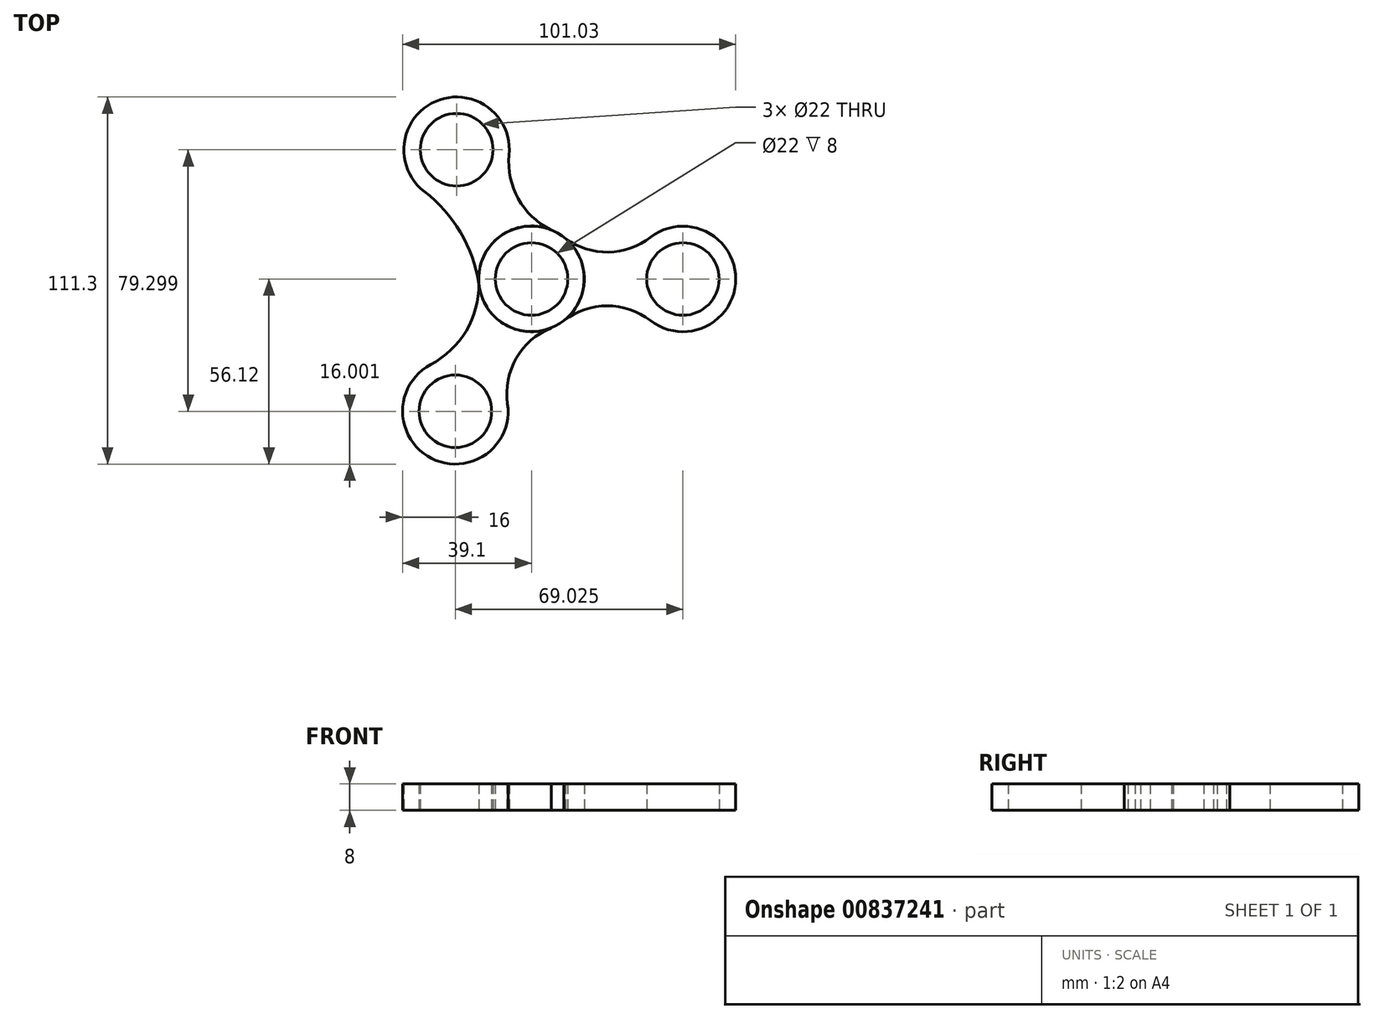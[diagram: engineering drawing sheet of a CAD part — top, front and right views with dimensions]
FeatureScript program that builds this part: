
annotation { "Feature Type Name" : "Feature", "Feature Type Description" : "" }
export const myFeature = defineFeature(function(context is Context, id is Id, definition is map)
    precondition{}
    {
        {
            var Q0;
            Q0=qCreatedBy(makeId("Top.planeOp"),FACE);
            var sketch = newSketch(context, id + "F0", { "sketchPlane" : qUnion([Q0])});
            skCircle(sketch, "E0", {"center": v(0, 0) * mm, "radius": 11 * mm});
            skCircle(sketch, "E1", {"center": v(45.93, 0) * mm, "radius": 11 * mm});
            skArc(sketch, "E2.0", {"start": v(36.13, -12.65) * mm, "mid": v(61.93, 0) * mm, "end": v(36.13, 12.65) * mm});
            skCircle(sketch, "E3.0", {"center": v(0, 0) * mm, "radius": 16 * mm});
            skArc(sketch, "E4", {"start": v(9.8, 12.65) * mm, "mid": v(22.96, 8.15) * mm, "end": v(36.13, 12.65) * mm});
            skArc(sketch, "E5", {"start": v(36.13, -12.65) * mm, "mid": v(22.96, -8.15) * mm, "end": v(9.8, -12.65) * mm});
            skCircle(sketch, "E6.1.4", {"center": v(-22.7, 39.18) * mm, "radius": 11 * mm});
            skArc(sketch, "E6.1.5", {"start": v(-6.79, 37.61) * mm, "mid": v(-29.05, 53.87) * mm, "end": v(-32.48, 26.51) * mm});
            skCircle(sketch, "E6.2.1", {"center": v(-0.02, 0.05) * mm, "radius": 16 * mm});
            skCircle(sketch, "E6.2.4", {"center": v(-23.1, -40.12) * mm, "radius": 11 * mm});
            skArc(sketch, "E6.2.5", {"start": v(-30.6, -25.98) * mm, "mid": v(-30.35, -54.38) * mm, "end": v(-7.26, -37.84) * mm});
            skArc(sketch, "E7", {"start": v(5.98, -14.84) * mm, "mid": v(-4.61, -24.05) * mm, "end": v(-7.26, -37.84) * mm});
            skArc(sketch, "E8", {"start": v(-30.6, -25.98) * mm, "mid": v(-19.49, -15.13) * mm, "end": v(-16.02, 0) * mm});
            skArc(sketch, "E9", {"start": v(-15.93, -1.63) * mm, "mid": v(-21.49, 14.04) * mm, "end": v(-32.48, 26.51) * mm});
            skArc(sketch, "E10", {"start": v(-6.79, 37.61) * mm, "mid": v(-4.04, 24.33) * mm, "end": v(5.78, 14.96) * mm});
            skSolve(sketch);
        }
        {
            var Q0;
            Q0=makeQuery(id+"F0.imprint","IMPRINT",FACE,{"disambiguationData":[TD([[makeQuery(id+"F0.imprint","IMPRINT",EDGE,{"derivedFrom":sQuery(id+"F0.wireOp",EDGE,"E6.1.4")}),-1.0]])]});
            var Q1;
            {var subQ6=sQuery(id+"F0.wireOp",EDGE,"E10");Q1=makeQuery(id+"F0.imprint","IMPRINT",FACE,{"disambiguationData":[TD([[makeQuery(id+"F0.imprint","IMPRINT",EDGE,{"derivedFrom":subQ6}),-1.0]])]});}
            var Q2;
            Q2=makeQuery(id+"F0.imprint","IMPRINT",FACE,{"disambiguationData":[TD([[makeQuery(id+"F0.imprint","IMPRINT",EDGE,{"derivedFrom":sQuery(id+"F0.wireOp",EDGE,"E0")}),-1.0]])]});
            var Q3;
            {var subQ0=sQuery(id+"F0.wireOp",EDGE,"E5");Q3=makeQuery(id+"F0.imprint","IMPRINT",FACE,{"disambiguationData":[TD([[makeQuery(id+"F0.imprint","IMPRINT",EDGE,{"derivedFrom":subQ0}),-1.0]])]});}
            var Q4;
            Q4=makeQuery(id+"F0.imprint","IMPRINT",FACE,{"disambiguationData":[TD([[makeQuery(id+"F0.imprint","IMPRINT",EDGE,{"derivedFrom":sQuery(id+"F0.wireOp",EDGE,"E1")}),-1.0]])]});
            var Q5;
            {var subQ0=sQuery(id+"F0.wireOp",EDGE,"E7");Q5=makeQuery(id+"F0.imprint","IMPRINT",FACE,{"disambiguationData":[TD([[makeQuery(id+"F0.imprint","IMPRINT",EDGE,{"derivedFrom":subQ0}),-1.0]])]});}
            var Q6;
            Q6=makeQuery(id+"F0.imprint","IMPRINT",FACE,{"disambiguationData":[TD([[makeQuery(id+"F0.imprint","IMPRINT",EDGE,{"derivedFrom":sQuery(id+"F0.wireOp",EDGE,"E6.2.4")}),-1.0]])]});
            extrude(context, id + "F1", {"entities" : qUnion([Q0, Q1, Q2, Q3, Q4, Q5, Q6]), "depth" : 8 * mm, "offsetDistance" : 25 * mm});
        }
    });
